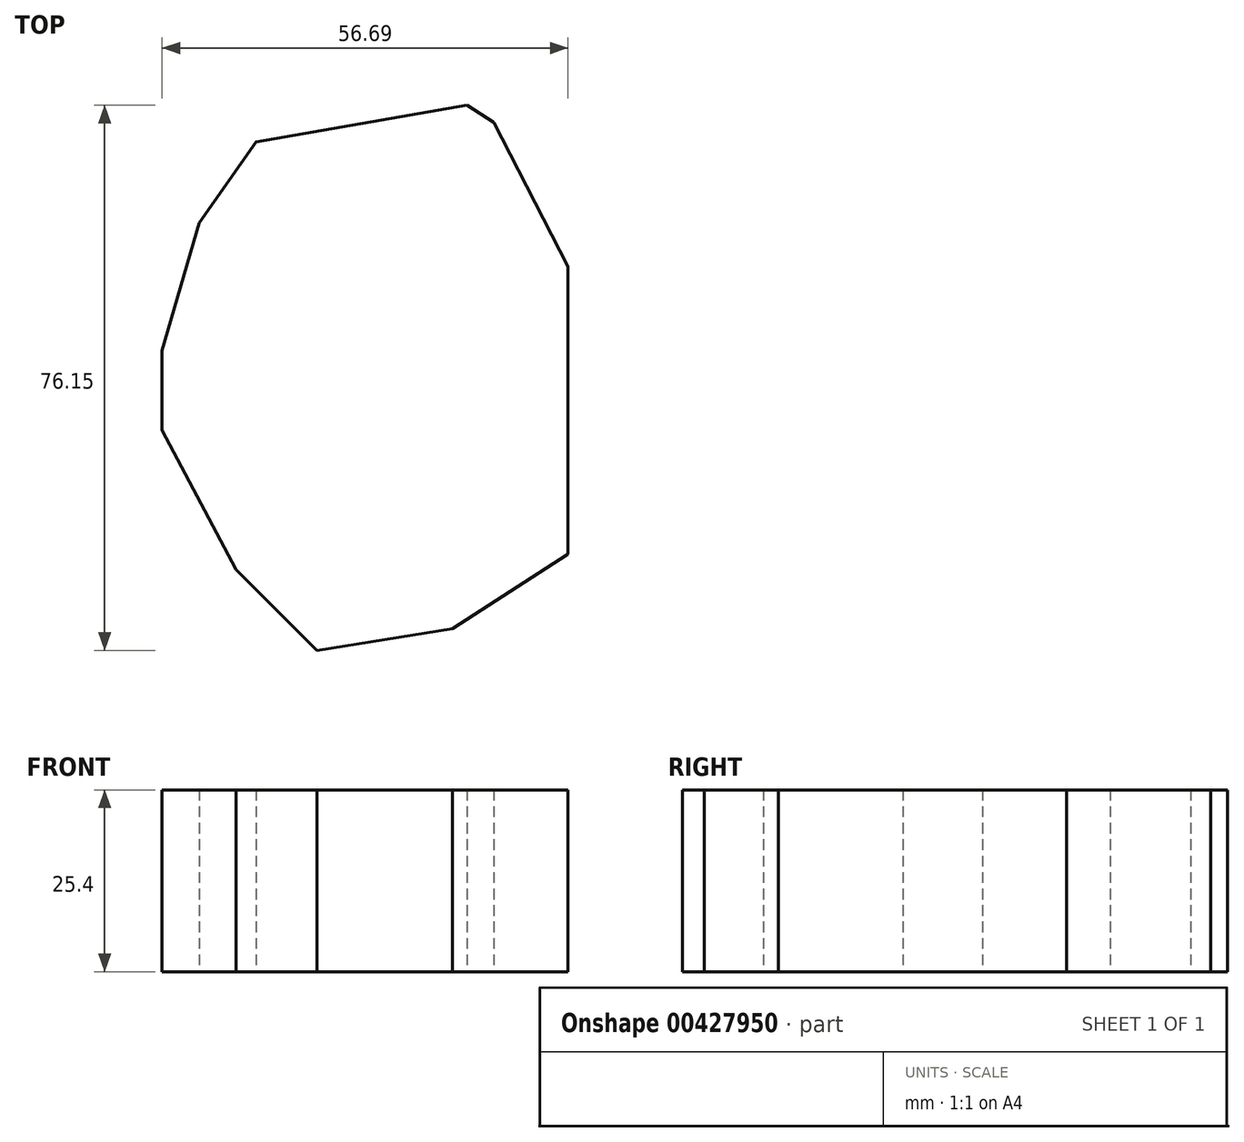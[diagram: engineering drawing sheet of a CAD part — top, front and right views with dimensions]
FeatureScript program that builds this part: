
annotation { "Feature Type Name" : "Feature", "Feature Type Description" : "" }
export const myFeature = defineFeature(function(context is Context, id is Id, definition is map)
    precondition{}
    {
        {
            var Q0;
            Q0=qCreatedBy(makeId("Top.planeOp"),FACE);
            var sketch = newSketch(context, id + "F0", { "sketchPlane" : qUnion([Q0])});
            skLineSegment(sketch, "E0", {"start": v(0, 44.65) * mm, "end": v(20.12, 31.85) * mm});
            skLineSegment(sketch, "E1", {"start": v(20.12, 31.85) * mm, "end": v(30.48, 11.73) * mm});
            skLineSegment(sketch, "E2", {"start": v(30.48, 11.73) * mm, "end": v(30.48, -4.11) * mm});
            skLineSegment(sketch, "E3", {"start": v(30.48, -4.11) * mm, "end": v(30.48, -28.5) * mm});
            skLineSegment(sketch, "E4", {"start": v(30.48, -28.5) * mm, "end": v(14.33, -38.86) * mm});
            skLineSegment(sketch, "E5", {"start": v(14.33, -38.86) * mm, "end": v(-4.57, -41.91) * mm});
            skLineSegment(sketch, "E6", {"start": v(-4.57, -41.91) * mm, "end": v(-15.85, -30.63) * mm});
            skLineSegment(sketch, "E7", {"start": v(-15.85, -30.63) * mm, "end": v(-26.21, -11.13) * mm});
            skLineSegment(sketch, "E8", {"start": v(-26.21, -11.13) * mm, "end": v(-26.21, 0) * mm});
            skLineSegment(sketch, "E9", {"start": v(-26.21, 0) * mm, "end": v(-21.03, 17.83) * mm});
            skLineSegment(sketch, "E10", {"start": v(-21.03, 17.83) * mm, "end": v(-13.1, 29.1) * mm});
            skLineSegment(sketch, "E11", {"start": v(-13.1, 29.1) * mm, "end": v(20.12, 34.9) * mm});
            skSolve(sketch);
        }
        {
            var Q0;
            Q0 = qSketchRegion(id + "F0", true);
            extrude(context, id + "F1", {"entities" : qUnion([Q0]), "depth" : 25.4 * mm});
        }
    });
